# Revit family: РД-50
name_source: partatom
category: Арматура трубопроводов
units: mm (PartAtom-declared; Revit-internal decimal feet)

## family parameters
Всегда вертикально = Да
На основе рабочей плоскости = Нет
Общий = Нет
При загрузке вырезать с полостями = Нет
Размер круглого соединителя = Использовать диаметр
Тип детали = Клапан - Вставляется

## types (10) — shared parameters
ADSK_Единица измерения = шт.
ADSK_Завод-изготовитель = РУП "БЕЛГАЗТЕХНИКА"
ADSK_Количество = 1
ADSK_Марка = РД-50
ADSK_Масса_Текст = 15,0 кг
ADSK_Материал наименование = АК-12 ГОСТ 1583-89
ADSK_Тип соединения = фланцевое 50-16-xx-1-B ГОСТ 33259-2015
zero-valued in all types: Отметка по умолчанию

## per-type parameters (varying)
| type | ADSK_Диапазоны настройки выходного давления, кПа | ADSK_Наименование |
| 1,6-2,0 - сбросной клапан- нет в комплекте | 1,6-2,0 | Регулятор РД-50-(1,6-2,0) ТУ BY 100270876.196-2018 |
| 1,8-3,0 - сбросной клапан- нет в комплекте | 1,8-3,0 | Регулятор РД-50-(1,8-3,0) ТУ BY 100270876.196-2018 |
| 2,8-5,0 - сбросной клапан- нет в комплекте | 2,8-5,0 | Регулятор РД-50-(2,8-5,0) ТУ BY 100270876.196-2018 |
| 4,8-7,0 - сбросной клапан- нет в комплекте | 4,8-7,0 | Регулятор РД-50-(4,8-7,0) ТУ BY 100270876.196-2018 |
| 6,8-13,0 - сбросной клапан - нет в комплекте | 6,8-13,0 | Регулятор РД-50-(6,8-13,0) ТУ BY 100270876.196-2018 |
| 1,6-2,0 - сбросной клапан встроен | 1,6-2,0 | Регулятор РД-50-С-(1,6-2,0) ТУ BY 100270876.196-2018 |
| 1,8-3,0 - сбросной клапан встроен | 1,8-3,0 | Регулятор РД-50-С-(1,8-3,0) ТУ BY 100270876.196-2018 |
| 2,8-5,0 - сбросной клапан встроен | 2,8-5,0 | Регулятор РД-50-С-(2,8-5,0) ТУ BY 100270876.196-2018 |
| 4,8-7,0 - сбросной клапан встроен | 4,8-7,0 | Регулятор РД-50-С-(4,8-7,0) ТУ BY 100270876.196-2018 |
| 6,8-13 - сбросной клапан встроен | 6,8-13,0 | Регулятор РД-50-С-(6,8-13,0) ТУ BY 100270876.196-2018 |
